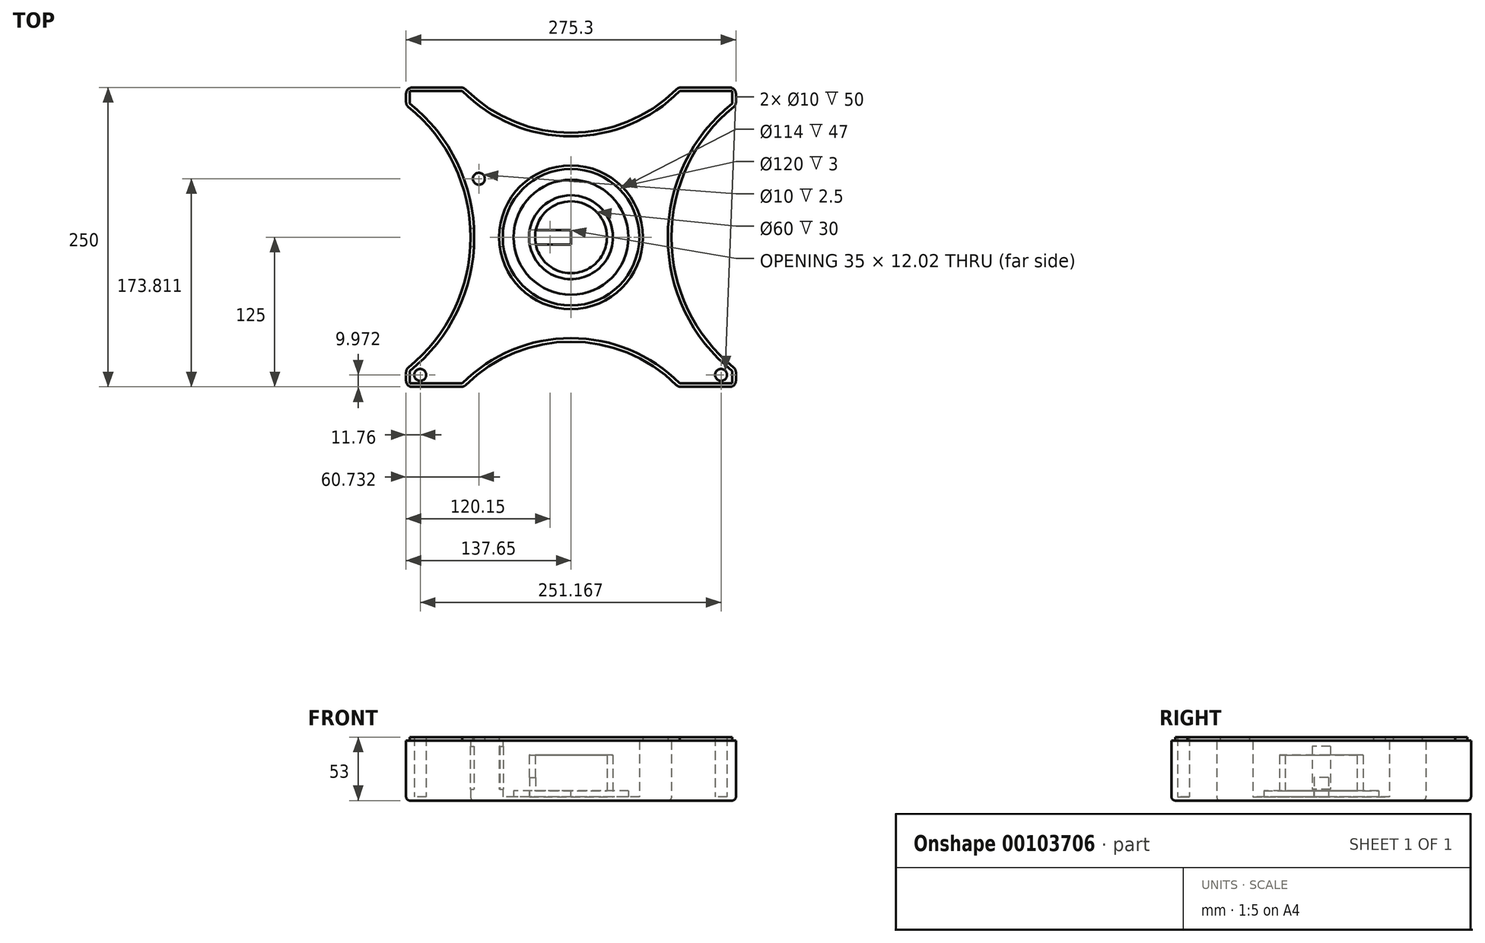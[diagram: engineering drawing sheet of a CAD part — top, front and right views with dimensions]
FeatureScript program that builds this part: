
annotation { "Feature Type Name" : "Feature", "Feature Type Description" : "" }
export const myFeature = defineFeature(function(context is Context, id is Id, definition is map)
    precondition{}
    {
        {
            var Q0;
            Q0=qCreatedBy(makeId("Top.planeOp"),FACE);
            var sketch = newSketch(context, id + "F0", { "sketchPlane" : qUnion([Q0])});
            skLineSegment(sketch, "E0.bottom", {"start": v(137.65, -125) * mm, "end": v(89.5, -125) * mm});
            skLineSegment(sketch, "E0.top", {"start": v(137.65, 125) * mm, "end": v(89.5, 125) * mm});
            skLineSegment(sketch, "E0.left", {"start": v(137.65, -125) * mm, "end": v(137.65, -110.32) * mm});
            skLineSegment(sketch, "E0.right", {"start": v(-137.65, -125) * mm, "end": v(-137.65, -110.32) * mm});
            skPoint(sketch, "E0.middle", {"position": v(0, 0) * mm});
            skArc(sketch, "E1", {"start": v(-137.65, -110.32) * mm, "mid": v(-83.85, 0) * mm, "end": v(-137.65, 110.32) * mm});
            skArc(sketch, "E2.MirrorCS", {"start": v(-137.65, 110.32) * mm, "mid": v(-83.85, 0) * mm, "end": v(-137.65, -110.32) * mm});
            skArc(sketch, "E3.MirrorCS", {"start": v(137.65, 110.32) * mm, "mid": v(83.85, 0) * mm, "end": v(137.65, -110.32) * mm});
            skArc(sketch, "E4", {"start": v(-89.5, 125) * mm, "mid": v(0, 87.26) * mm, "end": v(89.5, 125) * mm});
            skPoint(sketch, "E5", {"position": v(0, 125) * mm});
            skPoint(sketch, "E6.endSnap0", {"position": v(137.65, 0) * mm});
            skArc(sketch, "E7.MirrorCS", {"start": v(-89.5, -125) * mm, "mid": v(0, -87.26) * mm, "end": v(89.5, -125) * mm});
            skLineSegment(sketch, "E8.trimOffspring", {"start": v(-137.65, 110.32) * mm, "end": v(-137.65, 125) * mm});
            skLineSegment(sketch, "E9.trimOffspring", {"start": v(137.65, 110.32) * mm, "end": v(137.65, 125) * mm});
            skLineSegment(sketch, "E10.trimOffspring", {"start": v(-89.5, 125) * mm, "end": v(-137.65, 125) * mm});
            skLineSegment(sketch, "E11.trimOffspring", {"start": v(-89.5, -125) * mm, "end": v(-137.65, -125) * mm});
            skSolve(sketch);
        }
        {
            var Q0;
            Q0 = qSketchRegion(id + "F0", true);
            extrude(context, id + "F1", {"entities" : qUnion([Q0]), "depth" : 50 * mm});
        }
        {
            var Q0;
            Q0=makeQuery(id+"F1.opExtrude","CAP_FACE",FACE,{"disambiguationData":[OSD([sQuery(id+"F0.wireOp",EDGE,"E0.bottom"),sQuery(id+"F0.wireOp",EDGE,"E0.top"),sQuery(id+"F0.wireOp",EDGE,"E0.left"),sQuery(id+"F0.wireOp",EDGE,"E0.right"),sQuery(id+"F0.wireOp",EDGE,"E2.MirrorCS"),sQuery(id+"F0.wireOp",EDGE,"E3.MirrorCS"),sQuery(id+"F0.wireOp",EDGE,"E4"),sQuery(id+"F0.wireOp",EDGE,"E7.MirrorCS"),sQuery(id+"F0.wireOp",EDGE,"E8.trimOffspring"),sQuery(id+"F0.wireOp",EDGE,"E9.trimOffspring"),sQuery(id+"F0.wireOp",EDGE,"E10.trimOffspring"),sQuery(id+"F0.wireOp",EDGE,"E11.trimOffspring")])],"isStart":false});
            shell(context, id + "F2", {"entities" : qUnion([Q0]), "thickness" : 3 * mm});
        }
        {
            var Q0;
            Q0=makeQuery(id+"F1.opExtrude","SWEPT_EDGE",EDGE,{"disambiguationData":[OSD([sQuery(id+"F0.wireOp",EDGE,"E0.right"),sQuery(id+"F0.wireOp",EDGE,"E11.trimOffspring")])]});
            var Q1;
            Q1=makeQuery(id+"F1.opExtrude","SWEPT_EDGE",EDGE,{"disambiguationData":[OSD([sQuery(id+"F0.wireOp",EDGE,"E7.MirrorCS"),sQuery(id+"F0.wireOp",EDGE,"E11.trimOffspring")])]});
            var Q2;
            Q2=makeQuery(id+"F1.opExtrude","SWEPT_EDGE",EDGE,{"disambiguationData":[OSD([sQuery(id+"F0.wireOp",EDGE,"E0.bottom"),sQuery(id+"F0.wireOp",EDGE,"E7.MirrorCS")])]});
            var Q3;
            Q3=makeQuery(id+"F1.opExtrude","SWEPT_EDGE",EDGE,{"disambiguationData":[OSD([sQuery(id+"F0.wireOp",EDGE,"E0.bottom"),sQuery(id+"F0.wireOp",EDGE,"E0.left")])]});
            var Q4;
            Q4=makeQuery(id+"F1.opExtrude","SWEPT_EDGE",EDGE,{"disambiguationData":[OSD([sQuery(id+"F0.wireOp",EDGE,"E0.left"),sQuery(id+"F0.wireOp",EDGE,"E3.MirrorCS")])]});
            var Q5;
            Q5=makeQuery(id+"F1.opExtrude","SWEPT_EDGE",EDGE,{"disambiguationData":[OSD([sQuery(id+"F0.wireOp",EDGE,"E3.MirrorCS"),sQuery(id+"F0.wireOp",EDGE,"E9.trimOffspring")])]});
            var Q6;
            Q6=makeQuery(id+"F1.opExtrude","SWEPT_EDGE",EDGE,{"disambiguationData":[OSD([sQuery(id+"F0.wireOp",EDGE,"E0.top"),sQuery(id+"F0.wireOp",EDGE,"E9.trimOffspring")])]});
            var Q7;
            Q7=makeQuery(id+"F1.opExtrude","SWEPT_EDGE",EDGE,{"disambiguationData":[OSD([sQuery(id+"F0.wireOp",EDGE,"E0.top"),sQuery(id+"F0.wireOp",EDGE,"E4")])]});
            var Q8;
            Q8=makeQuery(id+"F1.opExtrude","SWEPT_EDGE",EDGE,{"disambiguationData":[OSD([sQuery(id+"F0.wireOp",EDGE,"E4"),sQuery(id+"F0.wireOp",EDGE,"E10.trimOffspring")])]});
            var Q9;
            Q9=makeQuery(id+"F1.opExtrude","SWEPT_EDGE",EDGE,{"disambiguationData":[OSD([sQuery(id+"F0.wireOp",EDGE,"E8.trimOffspring"),sQuery(id+"F0.wireOp",EDGE,"E10.trimOffspring")])]});
            var Q10;
            Q10=makeQuery(id+"F1.opExtrude","SWEPT_EDGE",EDGE,{"disambiguationData":[OSD([sQuery(id+"F0.wireOp",EDGE,"E2.MirrorCS"),sQuery(id+"F0.wireOp",EDGE,"E8.trimOffspring")])]});
            var Q11;
            Q11=makeQuery(id+"F1.opExtrude","SWEPT_EDGE",EDGE,{"disambiguationData":[OSD([sQuery(id+"F0.wireOp",EDGE,"E0.right"),sQuery(id+"F0.wireOp",EDGE,"E2.MirrorCS")])]});
            fillet(context, id + "F3", {"entities" : qUnion([Q0, Q1, Q2, Q3, Q4, Q5, Q6, Q7, Q8, Q9, Q10, Q11]), "radius" : 5 * mm, "tangentPropagation" : true, "allowEdgeOverflow" : false});
        }
        {
            var Q0;
            Q0=qCreatedBy(makeId("Top.planeOp"),FACE);
            var sketch = newSketch(context, id + "F4", { "sketchPlane" : qUnion([Q0])});
            skCircle(sketch, "E12", {"center": v(0, 0) * mm, "radius": 60 * mm});
            skSolve(sketch);
        }
        {
            var Q0;
            Q0 = qSketchRegion(id + "F4", true);
            extrude(context, id + "F5", {"entities" : qUnion([Q0]), "operationType" : NewBodyOperationType.ADD, "depth" : 50 * mm});
        }
        {
            var Q0;
            Q0=makeQuery(id+"F5.opExtrude","CAP_FACE",FACE,{"disambiguationData":[OSD([sQuery(id+"F4.wireOp",EDGE,"E12"),sQuery(id+"F4.wireOp",EDGE,"qJ9JI7Vv-458A-P813-C53i-Covv9JtIoCA3")])],"isStart":false});
            shell(context, id + "F6", {"entities" : qUnion([Q0]), "thickness" : 3 * mm});
        }
        {
            var Q0;
            Q0=qCreatedBy(makeId("Right.planeOp"),FACE);
            var sketch = newSketch(context, id + "F7", { "sketchPlane" : qUnion([Q0])});
            skLineSegment(sketch, "E13.bottom", {"start": v(7.59, 9.52) * mm, "end": v(-7.59, 9.52) * mm});
            skLineSegment(sketch, "E13.top", {"start": v(7.59, 45.42) * mm, "end": v(-7.59, 45.42) * mm});
            skLineSegment(sketch, "E13.left", {"start": v(7.59, 9.52) * mm, "end": v(7.59, 45.42) * mm});
            skLineSegment(sketch, "E13.right", {"start": v(-7.59, 9.52) * mm, "end": v(-7.59, 45.42) * mm});
            skPoint(sketch, "E13.middle", {"position": v(0, 27.47) * mm});
            skSolve(sketch);
        }
        {
            var Q0;
            Q0 = qSketchRegion(id + "F7", true);
            extrude(context, id + "F8", {"entities" : qUnion([Q0]), "operationType" : NewBodyOperationType.REMOVE, "oppositeDirection" : true, "depth" : 106.2 * mm});
        }
        {
            var Q0;
            Q0=makeQuery(id+"F2.opShell","OFFSET_FACE",FACE,{"disambiguationData":[OSD([sQuery(id+"F0.wireOp",EDGE,"E0.bottom"),sQuery(id+"F0.wireOp",EDGE,"E0.top"),sQuery(id+"F0.wireOp",EDGE,"E0.left"),sQuery(id+"F0.wireOp",EDGE,"E0.right"),sQuery(id+"F0.wireOp",EDGE,"E2.MirrorCS"),sQuery(id+"F0.wireOp",EDGE,"E3.MirrorCS"),sQuery(id+"F0.wireOp",EDGE,"E4"),sQuery(id+"F0.wireOp",EDGE,"E7.MirrorCS"),sQuery(id+"F0.wireOp",EDGE,"E8.trimOffspring"),sQuery(id+"F0.wireOp",EDGE,"E9.trimOffspring"),sQuery(id+"F0.wireOp",EDGE,"E10.trimOffspring"),sQuery(id+"F0.wireOp",EDGE,"E11.trimOffspring")])]});
            var sketch = newSketch(context, id + "F9", { "sketchPlane" : qUnion([Q0])});
            skCircle(sketch, "E14", {"center": v(-49.43, 76.92) * mm, "radius": 10 * mm});
            skCircle(sketch, "E15", {"center": v(-76.92, 48.81) * mm, "radius": 10 * mm});
            skCircle(sketch, "E16", {"center": v(-73.8, 13.66) * mm, "radius": 5.97 * mm});
            skCircle(sketch, "E17", {"center": v(-73.8, -13.66) * mm, "radius": 5.97 * mm});
            skCircle(sketch, "E18", {"center": v(49.43, 76.92) * mm, "radius": 10 * mm});
            skCircle(sketch, "E19", {"center": v(76.92, 48.81) * mm, "radius": 10 * mm});
            skSolve(sketch);
        }
        {
            var Q0;
            Q0 = qSketchRegion(id + "F9", true);
            extrude(context, id + "F10", {"entities" : qUnion([Q0]), "operationType" : NewBodyOperationType.ADD, "depth" : 50 * mm});
        }
        {
            var Q0;
            Q0=makeQuery(id+"F10.opExtrude","CAP_FACE",FACE,{"disambiguationData":[OSD([sQuery(id+"F9.wireOp",EDGE,"E15")])],"isStart":false});
            var sketch = newSketch(context, id + "F11", { "sketchPlane" : qUnion([Q0])});
            skCircle(sketch, "E20", {"center": v(-76.92, 48.81) * mm, "radius": 5 * mm});
            skSolve(sketch);
        }
        {
            var Q0;
            Q0 = qSketchRegion(id + "F11", true);
            extrude(context, id + "F12", {"entities" : qUnion([Q0]), "operationType" : NewBodyOperationType.REMOVE, "oppositeDirection" : true, "depth" : 2.5 * mm});
        }
        {
            var Q0;
            Q0=makeQuery(id+"F6.opShell","OFFSET_FACE",FACE,{"disambiguationData":[OSD([sQuery(id+"F0.wireOp",EDGE,"E0.bottom"),sQuery(id+"F0.wireOp",EDGE,"E0.top"),sQuery(id+"F0.wireOp",EDGE,"E0.left"),sQuery(id+"F0.wireOp",EDGE,"E0.right"),sQuery(id+"F0.wireOp",EDGE,"E2.MirrorCS"),sQuery(id+"F0.wireOp",EDGE,"E3.MirrorCS"),sQuery(id+"F0.wireOp",EDGE,"E4"),sQuery(id+"F0.wireOp",EDGE,"E7.MirrorCS"),sQuery(id+"F0.wireOp",EDGE,"E8.trimOffspring"),sQuery(id+"F0.wireOp",EDGE,"E9.trimOffspring"),sQuery(id+"F0.wireOp",EDGE,"E10.trimOffspring"),sQuery(id+"F0.wireOp",EDGE,"E11.trimOffspring")])]});
            var sketch = newSketch(context, id + "F13", { "sketchPlane" : qUnion([Q0])});
            skCircle(sketch, "E21", {"center": v(0, 0) * mm, "radius": 35 * mm});
            skSolve(sketch);
        }
        {
            var Q0;
            Q0 = qSketchRegion(id + "F13", true);
            extrude(context, id + "F14", {"entities" : qUnion([Q0]), "depth" : 35 * mm});
        }
        {
            var Q0;
            Q0=makeQuery(id+"F14.opExtrude","CAP_FACE",FACE,{"disambiguationData":[OSD([sQuery(id+"F13.wireOp",EDGE,"E21")])],"isStart":false});
            shell(context, id + "F15", {"entities" : qUnion([Q0]), "thickness" : 5 * mm});
        }
        {
            var Q0;
            Q0=makeQuery(id+"F6.opShell","OFFSET_FACE",FACE,{"disambiguationData":[OSD([sQuery(id+"F0.wireOp",EDGE,"E0.bottom"),sQuery(id+"F0.wireOp",EDGE,"E0.top"),sQuery(id+"F0.wireOp",EDGE,"E0.left"),sQuery(id+"F0.wireOp",EDGE,"E0.right"),sQuery(id+"F0.wireOp",EDGE,"E2.MirrorCS"),sQuery(id+"F0.wireOp",EDGE,"E3.MirrorCS"),sQuery(id+"F0.wireOp",EDGE,"E4"),sQuery(id+"F0.wireOp",EDGE,"E7.MirrorCS"),sQuery(id+"F0.wireOp",EDGE,"E8.trimOffspring"),sQuery(id+"F0.wireOp",EDGE,"E9.trimOffspring"),sQuery(id+"F0.wireOp",EDGE,"E10.trimOffspring"),sQuery(id+"F0.wireOp",EDGE,"E11.trimOffspring")])]});
            var sketch = newSketch(context, id + "F16", { "sketchPlane" : qUnion([Q0])});
            skCircle(sketch, "E22", {"center": v(0, 0) * mm, "radius": 48 * mm});
            skSolve(sketch);
        }
        {
            var Q0;
            Q0 = qSketchRegion(id + "F16", true);
            extrude(context, id + "F17", {"entities" : qUnion([Q0]), "depth" : 5 * mm});
        }
        {
            var Q0;
            Q0=makeQuery(id+"F2.opShell","OFFSET_FACE",FACE,{"disambiguationData":[OSD([sQuery(id+"F0.wireOp",EDGE,"E0.bottom"),sQuery(id+"F0.wireOp",EDGE,"E0.top"),sQuery(id+"F0.wireOp",EDGE,"E0.left"),sQuery(id+"F0.wireOp",EDGE,"E0.right"),sQuery(id+"F0.wireOp",EDGE,"E2.MirrorCS"),sQuery(id+"F0.wireOp",EDGE,"E3.MirrorCS"),sQuery(id+"F0.wireOp",EDGE,"E4"),sQuery(id+"F0.wireOp",EDGE,"E7.MirrorCS"),sQuery(id+"F0.wireOp",EDGE,"E8.trimOffspring"),sQuery(id+"F0.wireOp",EDGE,"E9.trimOffspring"),sQuery(id+"F0.wireOp",EDGE,"E10.trimOffspring"),sQuery(id+"F0.wireOp",EDGE,"E11.trimOffspring")])]});
            var sketch = newSketch(context, id + "F18", { "sketchPlane" : qUnion([Q0])});
            skCircle(sketch, "E23", {"center": v(-126.2, 115.32) * mm, "radius": 5 * mm});
            skCircle(sketch, "E24", {"center": v(126.2, 114.7) * mm, "radius": 5 * mm});
            skCircle(sketch, "E25.MirrorC", {"center": v(125.28, -115.03) * mm, "radius": 5 * mm});
            skCircle(sketch, "E26.MirrorC", {"center": v(-125.89, -115.03) * mm, "radius": 5 * mm});
            skSolve(sketch);
        }
        {
            var Q0;
            Q0=makeQuery(id+"F18.imprint","IMPRINT",FACE,{"disambiguationData":[TD([[makeQuery(id+"F18.imprint","IMPRINT",EDGE,{"derivedFrom":sQuery(id+"F18.wireOp",EDGE,"E23")}),1.0]])]});
            var Q1;
            Q1=makeQuery(id+"F18.imprint","IMPRINT",FACE,{"disambiguationData":[TD([[makeQuery(id+"F18.imprint","IMPRINT",EDGE,{"derivedFrom":sQuery(id+"F18.wireOp",EDGE,"E24")}),1.0]])]});
            var Q2;
            Q2=makeQuery(id+"F18.imprint","IMPRINT",FACE,{"disambiguationData":[TD([[makeQuery(id+"F18.imprint","IMPRINT",EDGE,{"derivedFrom":sQuery(id+"F18.wireOp",EDGE,"E26.MirrorC")}),-1.0]])]});
            var Q3;
            Q3=makeQuery(id+"F18.imprint","IMPRINT",FACE,{"disambiguationData":[TD([[makeQuery(id+"F18.imprint","IMPRINT",EDGE,{"derivedFrom":sQuery(id+"F18.wireOp",EDGE,"E25.MirrorC")}),-1.0]])]});
            extrude(context, id + "F19", {"entities" : qUnion([Q0, Q1, Q2, Q3]), "operationType" : NewBodyOperationType.ADD, "depth" : 50 * mm});
        }
        {
            var Q0;
            Q0=makeQuery(id+"F1.opExtrude","CAP_FACE",FACE,{"disambiguationData":[OSD([sQuery(id+"F0.wireOp",EDGE,"E0.bottom"),sQuery(id+"F0.wireOp",EDGE,"E0.top"),sQuery(id+"F0.wireOp",EDGE,"E0.left"),sQuery(id+"F0.wireOp",EDGE,"E0.right"),sQuery(id+"F0.wireOp",EDGE,"E2.MirrorCS"),sQuery(id+"F0.wireOp",EDGE,"E3.MirrorCS"),sQuery(id+"F0.wireOp",EDGE,"E4"),sQuery(id+"F0.wireOp",EDGE,"E7.MirrorCS"),sQuery(id+"F0.wireOp",EDGE,"E8.trimOffspring"),sQuery(id+"F0.wireOp",EDGE,"E9.trimOffspring"),sQuery(id+"F0.wireOp",EDGE,"E10.trimOffspring"),sQuery(id+"F0.wireOp",EDGE,"E11.trimOffspring")])],"isStart":true});
            var Q1;
            Q1=makeQuery(id+"F8.boolean.opBoolean","INTERSECT",EDGE,{"derivedFrom":[makeQuery(id+"F1.opExtrude","SWEPT_FACE",FACE,{"disambiguationData":[OSD([sQuery(id+"F0.wireOp",EDGE,"E2.MirrorCS")])]}),makeQuery(id+"F8.opExtrude","SWEPT_FACE",FACE,{"disambiguationData":[OSD([sQuery(id+"F7.wireOp",EDGE,"E13.left")])]})]});
            var Q2;
            Q2=makeQuery(id+"F8.boolean.opBoolean","INTERSECT",EDGE,{"derivedFrom":[makeQuery(id+"F1.opExtrude","SWEPT_FACE",FACE,{"disambiguationData":[OSD([sQuery(id+"F0.wireOp",EDGE,"E2.MirrorCS")])]}),makeQuery(id+"F8.opExtrude","SWEPT_FACE",FACE,{"disambiguationData":[OSD([sQuery(id+"F7.wireOp",EDGE,"E13.right")])]})]});
            var Q3;
            Q3=makeQuery(id+"F8.boolean.opBoolean","INTERSECT",EDGE,{"derivedFrom":[makeQuery(id+"F1.opExtrude","SWEPT_FACE",FACE,{"disambiguationData":[OSD([sQuery(id+"F0.wireOp",EDGE,"E2.MirrorCS")])]}),makeQuery(id+"F8.opExtrude","SWEPT_FACE",FACE,{"disambiguationData":[OSD([sQuery(id+"F7.wireOp",EDGE,"E13.top")])]})]});
            var Q4;
            Q4=makeQuery(id+"F8.boolean.opBoolean","INTERSECT",EDGE,{"derivedFrom":[makeQuery(id+"F1.opExtrude","SWEPT_FACE",FACE,{"disambiguationData":[OSD([sQuery(id+"F0.wireOp",EDGE,"E2.MirrorCS")])]}),makeQuery(id+"F8.opExtrude","SWEPT_FACE",FACE,{"disambiguationData":[OSD([sQuery(id+"F7.wireOp",EDGE,"E13.bottom")])]})]});
            fillet(context, id + "F20", {"entities" : qUnion([Q0, Q1, Q2, Q3, Q4]), "radius" : 3 * mm, "tangentPropagation" : true, "allowEdgeOverflow" : false});
        }
        {
            var Q0;
            Q0=qCreatedBy(makeId("Right.planeOp"),FACE);
            var sketch = newSketch(context, id + "F21", { "sketchPlane" : qUnion([Q0])});
            skLineSegment(sketch, "E27.bottom", {"start": v(6.01, -19.35) * mm, "end": v(-6.01, -19.35) * mm});
            skLineSegment(sketch, "E27.top", {"start": v(6.01, 19.35) * mm, "end": v(-6.01, 19.35) * mm});
            skLineSegment(sketch, "E27.left", {"start": v(6.01, -19.35) * mm, "end": v(6.01, 19.35) * mm});
            skLineSegment(sketch, "E27.right", {"start": v(-6.01, -19.35) * mm, "end": v(-6.01, 19.35) * mm});
            skPoint(sketch, "E27.middle", {"position": v(0, 0) * mm});
            skSolve(sketch);
        }
        {
            var Q0;
            Q0 = qSketchRegion(id + "F21", true);
            var Q1;
            Q1=makeQuery(id+"F14.opExtrude","SWEPT_BODY",BODY,{"disambiguationData":[OSD([sQuery(id+"F13.wireOp",EDGE,"E21")])]});
            extrude(context, id + "F22", {"entities" : qUnion([Q0]), "operationType" : NewBodyOperationType.REMOVE, "endBound" : BoundingType.UP_TO_BODY, "oppositeDirection" : true, "endBoundEntityBody" : qUnion([Q1]), "depth" : 25 * mm});
        }
    });
